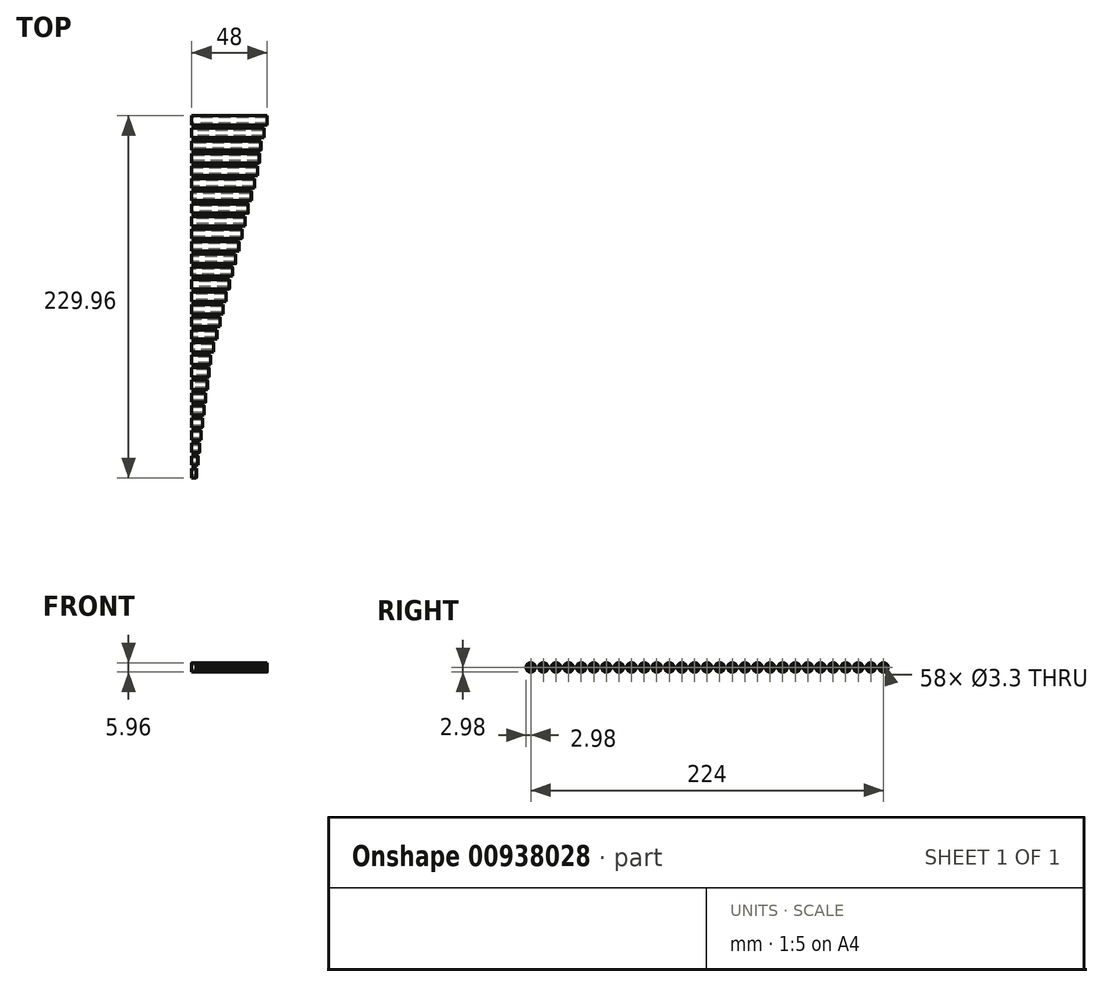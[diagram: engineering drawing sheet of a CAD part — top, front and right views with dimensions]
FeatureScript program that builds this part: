
annotation { "Feature Type Name" : "Feature", "Feature Type Description" : "" }
export const myFeature = defineFeature(function(context is Context, id is Id, definition is map)
    precondition{}
    {
        {
            var Q0;
            Q0=qCreatedBy(makeId("Right.planeOp"),FACE);
            var sketch = newSketch(context, id + "F0", { "sketchPlane" : qUnion([Q0]) });
            skCircle(sketch, "E0", {"center": v(0, 0) * mm, "radius": 1.65 * mm});
            skCircle(sketch, "E1", {"center": v(0, 0) * mm, "radius": 2.98 * mm});
            skSolve(sketch);
        }
        {
            var Q0;
            Q0=qSketchRegion(id+"F0",true);
            extrude(context, id + "F1", {"entities" : qUnion([Q0]), "depth" : 3 * mm, "offsetDistance" : 25 * mm});
        }
        {
            var Q0;
            Q0=qSketchRegion(id+"F0",true);
            extrude(context, id + "F2", {"entities" : qUnion([Q0]), "depth" : 4 * mm, "offsetDistance" : 25 * mm});
        }
        {
            var Q0;
            Q0=qSketchRegion(id+"F0",true);
            extrude(context, id + "F3", {"entities" : qUnion([Q0]), "depth" : 5 * mm, "offsetDistance" : 25 * mm});
        }
        {
            var Q0;
            Q0=qSketchRegion(id+"F0",true);
            extrude(context, id + "F4", {"entities" : qUnion([Q0]), "depth" : 6 * mm, "offsetDistance" : 25 * mm});
        }
        {
            var Q0;
            Q0=qSketchRegion(id+"F0",true);
            extrude(context, id + "F5", {"entities" : qUnion([Q0]), "depth" : 7 * mm, "offsetDistance" : 25 * mm});
        }
        {
            var Q0;
            Q0=qSketchRegion(id+"F0",true);
            extrude(context, id + "F6", {"entities" : qUnion([Q0]), "depth" : 8 * mm, "offsetDistance" : 25 * mm});
        }
        {
            var Q0;
            Q0=qSketchRegion(id+"F0",true);
            extrude(context, id + "F7", {"entities" : qUnion([Q0]), "depth" : 9 * mm, "offsetDistance" : 25 * mm});
        }
        {
            var Q0;
            Q0=qSketchRegion(id+"F0",true);
            extrude(context, id + "F8", {"entities" : qUnion([Q0]), "depth" : 10 * mm, "offsetDistance" : 25 * mm});
        }
        {
            var Q0;
            Q0=qSketchRegion(id+"F0",true);
            extrude(context, id + "F9", {"entities" : qUnion([Q0]), "depth" : 11 * mm, "offsetDistance" : 25 * mm});
        }
        {
            var Q0;
            Q0=qSketchRegion(id+"F0",true);
            extrude(context, id + "F10", {"entities" : qUnion([Q0]), "depth" : 12 * mm, "offsetDistance" : 25 * mm});
        }
        {
            var Q0;
            Q0=qSketchRegion(id+"F0",true);
            extrude(context, id + "F11", {"entities" : qUnion([Q0]), "depth" : 14 * mm, "offsetDistance" : 25 * mm});
        }
        {
            var Q0;
            Q0=qSketchRegion(id+"F0",true);
            extrude(context, id + "F12", {"entities" : qUnion([Q0]), "depth" : 16 * mm, "offsetDistance" : 25 * mm});
        }
        {
            var Q0;
            Q0=qSketchRegion(id+"F0",true);
            extrude(context, id + "F13", {"entities" : qUnion([Q0]), "depth" : 18 * mm, "offsetDistance" : 25 * mm});
        }
        {
            var Q0;
            Q0=qSketchRegion(id+"F0",true);
            extrude(context, id + "F14", {"entities" : qUnion([Q0]), "depth" : 20 * mm, "offsetDistance" : 25 * mm});
        }
        {
            var Q0;
            Q0=qSketchRegion(id+"F0",true);
            extrude(context, id + "F15", {"entities" : qUnion([Q0]), "depth" : 22 * mm, "offsetDistance" : 25 * mm});
        }
        {
            var Q0;
            Q0=qSketchRegion(id+"F0",true);
            extrude(context, id + "F16", {"entities" : qUnion([Q0]), "depth" : 24 * mm, "offsetDistance" : 25 * mm});
        }
        {
            var Q0;
            Q0=qSketchRegion(id+"F0",true);
            extrude(context, id + "F17", {"entities" : qUnion([Q0]), "depth" : 26 * mm, "offsetDistance" : 25 * mm});
        }
        {
            var Q0;
            Q0=qSketchRegion(id+"F0",true);
            extrude(context, id + "F18", {"entities" : qUnion([Q0]), "depth" : 28 * mm, "offsetDistance" : 25 * mm});
        }
        {
            var Q0;
            Q0=qSketchRegion(id+"F0",true);
            extrude(context, id + "F19", {"entities" : qUnion([Q0]), "depth" : 30 * mm, "offsetDistance" : 25 * mm});
        }
        {
            var Q0;
            Q0=qSketchRegion(id+"F0",true);
            extrude(context, id + "F20", {"entities" : qUnion([Q0]), "depth" : 32 * mm, "offsetDistance" : 25 * mm});
        }
        {
            var Q0;
            Q0=qSketchRegion(id+"F0",true);
            extrude(context, id + "F21", {"entities" : qUnion([Q0]), "depth" : 34 * mm, "offsetDistance" : 25 * mm});
        }
        {
            var Q0;
            Q0=qSketchRegion(id+"F0",true);
            extrude(context, id + "F22", {"entities" : qUnion([Q0]), "depth" : 36 * mm, "offsetDistance" : 25 * mm});
        }
        {
            var Q0;
            Q0=qSketchRegion(id+"F0",true);
            extrude(context, id + "F23", {"entities" : qUnion([Q0]), "depth" : 38 * mm, "offsetDistance" : 25 * mm});
        }
        {
            var Q0;
            Q0=qSketchRegion(id+"F0",true);
            extrude(context, id + "F24", {"entities" : qUnion([Q0]), "depth" : 40 * mm, "offsetDistance" : 25 * mm});
        }
        {
            var Q0;
            Q0=qSketchRegion(id+"F0",true);
            extrude(context, id + "F25", {"entities" : qUnion([Q0]), "depth" : 42 * mm, "offsetDistance" : 25 * mm});
        }
        {
            var Q0;
            Q0=qSketchRegion(id+"F0",true);
            extrude(context, id + "F26", {"entities" : qUnion([Q0]), "depth" : 43 * mm, "offsetDistance" : 25 * mm});
        }
        {
            var Q0;
            Q0=qSketchRegion(id+"F0",true);
            extrude(context, id + "F27", {"entities" : qUnion([Q0]), "depth" : 44 * mm, "offsetDistance" : 25 * mm});
        }
        {
            var Q0;
            Q0=qSketchRegion(id+"F0",true);
            extrude(context, id + "F28", {"entities" : qUnion([Q0]), "depth" : 46 * mm, "offsetDistance" : 25 * mm});
        }
        {
            var Q0;
            Q0=qSketchRegion(id+"F0",true);
            extrude(context, id + "F29", {"entities" : qUnion([Q0]), "depth" : 48 * mm, "offsetDistance" : 25 * mm});
        }
        {
            var Q0;
            Q0=makeQuery(id+"F1.opExtrude","CAP_EDGE",EDGE,{"disambiguationData":[OSD([sQuery(id+"F0.wireOp",EDGE,"E0")])],"isStart":false});
            var Q1;
            Q1=makeQuery(id+"F2.opExtrude","SWEPT_FACE",FACE,{"disambiguationData":[OSD([sQuery(id+"F0.wireOp",EDGE,"E0")])]});
            var Q2;
            Q2=makeQuery(id+"F3.opExtrude","CAP_EDGE",EDGE,{"disambiguationData":[OSD([sQuery(id+"F0.wireOp",EDGE,"E0")])],"isStart":false});
            var Q3;
            Q3=makeQuery(id+"F1.opExtrude","CAP_EDGE",EDGE,{"disambiguationData":[OSD([sQuery(id+"F0.wireOp",EDGE,"E0")])],"isStart":true});
            var Q4;
            Q4=makeQuery(id+"F3.opExtrude","CAP_EDGE",EDGE,{"disambiguationData":[OSD([sQuery(id+"F0.wireOp",EDGE,"E0")])],"isStart":true});
            var Q5;
            Q5=makeQuery(id+"F4.opExtrude","CAP_EDGE",EDGE,{"disambiguationData":[OSD([sQuery(id+"F0.wireOp",EDGE,"E0")])],"isStart":true});
            var Q6;
            Q6=makeQuery(id+"F4.opExtrude","CAP_EDGE",EDGE,{"disambiguationData":[OSD([sQuery(id+"F0.wireOp",EDGE,"E0")])],"isStart":false});
            var Q7;
            Q7=makeQuery(id+"F5.opExtrude","CAP_EDGE",EDGE,{"disambiguationData":[OSD([sQuery(id+"F0.wireOp",EDGE,"E0")])],"isStart":false});
            var Q8;
            Q8=makeQuery(id+"F5.opExtrude","CAP_EDGE",EDGE,{"disambiguationData":[OSD([sQuery(id+"F0.wireOp",EDGE,"E0")])],"isStart":true});
            var Q9;
            Q9=makeQuery(id+"F6.opExtrude","CAP_EDGE",EDGE,{"disambiguationData":[OSD([sQuery(id+"F0.wireOp",EDGE,"E0")])],"isStart":true});
            var Q10;
            Q10=makeQuery(id+"F6.opExtrude","CAP_EDGE",EDGE,{"disambiguationData":[OSD([sQuery(id+"F0.wireOp",EDGE,"E0")])],"isStart":false});
            var Q11;
            Q11=makeQuery(id+"F7.opExtrude","CAP_EDGE",EDGE,{"disambiguationData":[OSD([sQuery(id+"F0.wireOp",EDGE,"E0")])],"isStart":false});
            var Q12;
            Q12=makeQuery(id+"F7.opExtrude","CAP_EDGE",EDGE,{"disambiguationData":[OSD([sQuery(id+"F0.wireOp",EDGE,"E0")])],"isStart":true});
            var Q13;
            Q13=makeQuery(id+"F8.opExtrude","CAP_EDGE",EDGE,{"disambiguationData":[OSD([sQuery(id+"F0.wireOp",EDGE,"E0")])],"isStart":true});
            var Q14;
            Q14=makeQuery(id+"F8.opExtrude","CAP_EDGE",EDGE,{"disambiguationData":[OSD([sQuery(id+"F0.wireOp",EDGE,"E0")])],"isStart":false});
            var Q15;
            Q15=makeQuery(id+"F9.opExtrude","CAP_EDGE",EDGE,{"disambiguationData":[OSD([sQuery(id+"F0.wireOp",EDGE,"E0")])],"isStart":false});
            var Q16;
            Q16=makeQuery(id+"F9.opExtrude","CAP_EDGE",EDGE,{"disambiguationData":[OSD([sQuery(id+"F0.wireOp",EDGE,"E0")])],"isStart":true});
            var Q17;
            Q17=makeQuery(id+"F10.opExtrude","CAP_EDGE",EDGE,{"disambiguationData":[OSD([sQuery(id+"F0.wireOp",EDGE,"E0")])],"isStart":true});
            var Q18;
            Q18=makeQuery(id+"F10.opExtrude","CAP_EDGE",EDGE,{"disambiguationData":[OSD([sQuery(id+"F0.wireOp",EDGE,"E0")])],"isStart":false});
            var Q19;
            Q19=makeQuery(id+"F11.opExtrude","CAP_EDGE",EDGE,{"disambiguationData":[OSD([sQuery(id+"F0.wireOp",EDGE,"E0")])],"isStart":false});
            var Q20;
            Q20=makeQuery(id+"F11.opExtrude","CAP_EDGE",EDGE,{"disambiguationData":[OSD([sQuery(id+"F0.wireOp",EDGE,"E0")])],"isStart":true});
            var Q21;
            Q21=makeQuery(id+"F12.opExtrude","CAP_EDGE",EDGE,{"disambiguationData":[OSD([sQuery(id+"F0.wireOp",EDGE,"E0")])],"isStart":true});
            var Q22;
            Q22=makeQuery(id+"F12.opExtrude","CAP_EDGE",EDGE,{"disambiguationData":[OSD([sQuery(id+"F0.wireOp",EDGE,"E0")])],"isStart":false});
            var Q23;
            Q23=makeQuery(id+"F13.opExtrude","CAP_EDGE",EDGE,{"disambiguationData":[OSD([sQuery(id+"F0.wireOp",EDGE,"E0")])],"isStart":false});
            var Q24;
            Q24=makeQuery(id+"F13.opExtrude","CAP_EDGE",EDGE,{"disambiguationData":[OSD([sQuery(id+"F0.wireOp",EDGE,"E0")])],"isStart":true});
            var Q25;
            Q25=makeQuery(id+"F14.opExtrude","CAP_EDGE",EDGE,{"disambiguationData":[OSD([sQuery(id+"F0.wireOp",EDGE,"E0")])],"isStart":true});
            var Q26;
            Q26=makeQuery(id+"F14.opExtrude","CAP_EDGE",EDGE,{"disambiguationData":[OSD([sQuery(id+"F0.wireOp",EDGE,"E0")])],"isStart":false});
            var Q27;
            Q27=makeQuery(id+"F15.opExtrude","CAP_EDGE",EDGE,{"disambiguationData":[OSD([sQuery(id+"F0.wireOp",EDGE,"E0")])],"isStart":false});
            var Q28;
            Q28=makeQuery(id+"F15.opExtrude","CAP_EDGE",EDGE,{"disambiguationData":[OSD([sQuery(id+"F0.wireOp",EDGE,"E0")])],"isStart":true});
            var Q29;
            Q29=makeQuery(id+"F16.opExtrude","CAP_EDGE",EDGE,{"disambiguationData":[OSD([sQuery(id+"F0.wireOp",EDGE,"E0")])],"isStart":true});
            var Q30;
            Q30=makeQuery(id+"F16.opExtrude","CAP_EDGE",EDGE,{"disambiguationData":[OSD([sQuery(id+"F0.wireOp",EDGE,"E0")])],"isStart":false});
            var Q31;
            Q31=makeQuery(id+"F17.opExtrude","CAP_EDGE",EDGE,{"disambiguationData":[OSD([sQuery(id+"F0.wireOp",EDGE,"E0")])],"isStart":false});
            var Q32;
            Q32=makeQuery(id+"F17.opExtrude","CAP_EDGE",EDGE,{"disambiguationData":[OSD([sQuery(id+"F0.wireOp",EDGE,"E0")])],"isStart":true});
            var Q33;
            Q33=makeQuery(id+"F18.opExtrude","CAP_EDGE",EDGE,{"disambiguationData":[OSD([sQuery(id+"F0.wireOp",EDGE,"E0")])],"isStart":true});
            var Q34;
            Q34=makeQuery(id+"F18.opExtrude","CAP_EDGE",EDGE,{"disambiguationData":[OSD([sQuery(id+"F0.wireOp",EDGE,"E0")])],"isStart":false});
            var Q35;
            Q35=makeQuery(id+"F19.opExtrude","CAP_EDGE",EDGE,{"disambiguationData":[OSD([sQuery(id+"F0.wireOp",EDGE,"E0")])],"isStart":false});
            var Q36;
            Q36=makeQuery(id+"F19.opExtrude","CAP_EDGE",EDGE,{"disambiguationData":[OSD([sQuery(id+"F0.wireOp",EDGE,"E0")])],"isStart":true});
            var Q37;
            Q37=makeQuery(id+"F20.opExtrude","CAP_EDGE",EDGE,{"disambiguationData":[OSD([sQuery(id+"F0.wireOp",EDGE,"E0")])],"isStart":true});
            var Q38;
            Q38=makeQuery(id+"F20.opExtrude","CAP_EDGE",EDGE,{"disambiguationData":[OSD([sQuery(id+"F0.wireOp",EDGE,"E0")])],"isStart":false});
            var Q39;
            Q39=makeQuery(id+"F21.opExtrude","CAP_EDGE",EDGE,{"disambiguationData":[OSD([sQuery(id+"F0.wireOp",EDGE,"E0")])],"isStart":false});
            var Q40;
            Q40=makeQuery(id+"F21.opExtrude","CAP_EDGE",EDGE,{"disambiguationData":[OSD([sQuery(id+"F0.wireOp",EDGE,"E0")])],"isStart":true});
            var Q41;
            Q41=makeQuery(id+"F22.opExtrude","CAP_EDGE",EDGE,{"disambiguationData":[OSD([sQuery(id+"F0.wireOp",EDGE,"E0")])],"isStart":true});
            var Q42;
            Q42=makeQuery(id+"F22.opExtrude","CAP_EDGE",EDGE,{"disambiguationData":[OSD([sQuery(id+"F0.wireOp",EDGE,"E0")])],"isStart":false});
            var Q43;
            Q43=makeQuery(id+"F23.opExtrude","CAP_EDGE",EDGE,{"disambiguationData":[OSD([sQuery(id+"F0.wireOp",EDGE,"E0")])],"isStart":false});
            var Q44;
            Q44=makeQuery(id+"F23.opExtrude","CAP_EDGE",EDGE,{"disambiguationData":[OSD([sQuery(id+"F0.wireOp",EDGE,"E0")])],"isStart":true});
            var Q45;
            Q45=makeQuery(id+"F24.opExtrude","CAP_EDGE",EDGE,{"disambiguationData":[OSD([sQuery(id+"F0.wireOp",EDGE,"E0")])],"isStart":true});
            var Q46;
            Q46=makeQuery(id+"F24.opExtrude","SWEPT_FACE",FACE,{"disambiguationData":[OSD([sQuery(id+"F0.wireOp",EDGE,"E0")])]});
            var Q47;
            Q47=makeQuery(id+"F25.opExtrude","CAP_EDGE",EDGE,{"disambiguationData":[OSD([sQuery(id+"F0.wireOp",EDGE,"E0")])],"isStart":false});
            var Q48;
            Q48=makeQuery(id+"F25.opExtrude","CAP_EDGE",EDGE,{"disambiguationData":[OSD([sQuery(id+"F0.wireOp",EDGE,"E0")])],"isStart":true});
            var Q49;
            Q49=makeQuery(id+"F26.opExtrude","CAP_EDGE",EDGE,{"disambiguationData":[OSD([sQuery(id+"F0.wireOp",EDGE,"E0")])],"isStart":true});
            var Q50;
            Q50=makeQuery(id+"F26.opExtrude","CAP_EDGE",EDGE,{"disambiguationData":[OSD([sQuery(id+"F0.wireOp",EDGE,"E0")])],"isStart":false});
            var Q51;
            Q51=makeQuery(id+"F27.opExtrude","CAP_EDGE",EDGE,{"disambiguationData":[OSD([sQuery(id+"F0.wireOp",EDGE,"E0")])],"isStart":false});
            var Q52;
            Q52=makeQuery(id+"F27.opExtrude","CAP_EDGE",EDGE,{"disambiguationData":[OSD([sQuery(id+"F0.wireOp",EDGE,"E0")])],"isStart":true});
            var Q53;
            Q53=makeQuery(id+"F28.opExtrude","CAP_EDGE",EDGE,{"disambiguationData":[OSD([sQuery(id+"F0.wireOp",EDGE,"E0")])],"isStart":true});
            var Q54;
            Q54=makeQuery(id+"F28.opExtrude","CAP_EDGE",EDGE,{"disambiguationData":[OSD([sQuery(id+"F0.wireOp",EDGE,"E0")])],"isStart":false});
            var Q55;
            Q55=makeQuery(id+"F29.opExtrude","CAP_EDGE",EDGE,{"disambiguationData":[OSD([sQuery(id+"F0.wireOp",EDGE,"E0")])],"isStart":false});
            var Q56;
            Q56=makeQuery(id+"F29.opExtrude","CAP_EDGE",EDGE,{"disambiguationData":[OSD([sQuery(id+"F0.wireOp",EDGE,"E0")])],"isStart":true});
            chamfer(context, id + "F30", {"entities" : qUnion([Q0, Q1, Q2, Q3, Q4, Q5, Q6, Q7, Q8, Q9, Q10, Q11, Q12, Q13, Q14, Q15, Q16, Q17, Q18, Q19, Q20, Q21, Q22, Q23, Q24, Q25, Q26, Q27, Q28, Q29, Q30, Q31, Q32, Q33, Q34, Q35, Q36, Q37, Q38, Q39, Q40, Q41, Q42, Q43, Q44, Q45, Q46, Q47, Q48, Q49, Q50, Q51, Q52, Q53, Q54, Q55, Q56]), "width" : 0.35 * mm, "tangentPropagation" : true});
        }
        {
            var Q0;
            Q0=makeQuery(id+"F29.opExtrude","CAP_EDGE",EDGE,{"disambiguationData":[OSD([sQuery(id+"F0.wireOp",EDGE,"E1")])],"isStart":false});
            var Q1;
            Q1=makeQuery(id+"F28.opExtrude","CAP_EDGE",EDGE,{"disambiguationData":[OSD([sQuery(id+"F0.wireOp",EDGE,"E1")])],"isStart":false});
            var Q2;
            Q2=makeQuery(id+"F27.opExtrude","CAP_EDGE",EDGE,{"disambiguationData":[OSD([sQuery(id+"F0.wireOp",EDGE,"E1")])],"isStart":false});
            var Q3;
            Q3=makeQuery(id+"F26.opExtrude","CAP_EDGE",EDGE,{"disambiguationData":[OSD([sQuery(id+"F0.wireOp",EDGE,"E1")])],"isStart":false});
            var Q4;
            Q4=makeQuery(id+"F25.opExtrude","CAP_EDGE",EDGE,{"disambiguationData":[OSD([sQuery(id+"F0.wireOp",EDGE,"E1")])],"isStart":false});
            var Q5;
            Q5=makeQuery(id+"F24.opExtrude","CAP_EDGE",EDGE,{"disambiguationData":[OSD([sQuery(id+"F0.wireOp",EDGE,"E1")])],"isStart":false});
            var Q6;
            Q6=makeQuery(id+"F23.opExtrude","CAP_EDGE",EDGE,{"disambiguationData":[OSD([sQuery(id+"F0.wireOp",EDGE,"E1")])],"isStart":false});
            var Q7;
            Q7=makeQuery(id+"F22.opExtrude","CAP_EDGE",EDGE,{"disambiguationData":[OSD([sQuery(id+"F0.wireOp",EDGE,"E1")])],"isStart":false});
            var Q8;
            Q8=makeQuery(id+"F21.opExtrude","CAP_EDGE",EDGE,{"disambiguationData":[OSD([sQuery(id+"F0.wireOp",EDGE,"E1")])],"isStart":false});
            var Q9;
            Q9=makeQuery(id+"F20.opExtrude","CAP_EDGE",EDGE,{"disambiguationData":[OSD([sQuery(id+"F0.wireOp",EDGE,"E1")])],"isStart":false});
            var Q10;
            Q10=makeQuery(id+"F19.opExtrude","CAP_EDGE",EDGE,{"disambiguationData":[OSD([sQuery(id+"F0.wireOp",EDGE,"E1")])],"isStart":false});
            var Q11;
            Q11=makeQuery(id+"F18.opExtrude","CAP_EDGE",EDGE,{"disambiguationData":[OSD([sQuery(id+"F0.wireOp",EDGE,"E1")])],"isStart":false});
            var Q12;
            Q12=makeQuery(id+"F17.opExtrude","CAP_EDGE",EDGE,{"disambiguationData":[OSD([sQuery(id+"F0.wireOp",EDGE,"E1")])],"isStart":false});
            var Q13;
            Q13=makeQuery(id+"F16.opExtrude","CAP_EDGE",EDGE,{"disambiguationData":[OSD([sQuery(id+"F0.wireOp",EDGE,"E1")])],"isStart":false});
            var Q14;
            Q14=makeQuery(id+"F15.opExtrude","CAP_EDGE",EDGE,{"disambiguationData":[OSD([sQuery(id+"F0.wireOp",EDGE,"E1")])],"isStart":false});
            var Q15;
            Q15=makeQuery(id+"F14.opExtrude","CAP_EDGE",EDGE,{"disambiguationData":[OSD([sQuery(id+"F0.wireOp",EDGE,"E1")])],"isStart":false});
            var Q16;
            Q16=makeQuery(id+"F24.opExtrude","SWEPT_FACE",FACE,{"disambiguationData":[OSD([sQuery(id+"F0.wireOp",EDGE,"E1")])]});
            var Q17;
            Q17=makeQuery(id+"F12.opExtrude","CAP_EDGE",EDGE,{"disambiguationData":[OSD([sQuery(id+"F0.wireOp",EDGE,"E1")])],"isStart":false});
            var Q18;
            Q18=makeQuery(id+"F13.opExtrude","CAP_EDGE",EDGE,{"disambiguationData":[OSD([sQuery(id+"F0.wireOp",EDGE,"E1")])],"isStart":false});
            var Q19;
            Q19=makeQuery(id+"F11.opExtrude","CAP_EDGE",EDGE,{"disambiguationData":[OSD([sQuery(id+"F0.wireOp",EDGE,"E1")])],"isStart":false});
            var Q20;
            Q20=makeQuery(id+"F10.opExtrude","CAP_EDGE",EDGE,{"disambiguationData":[OSD([sQuery(id+"F0.wireOp",EDGE,"E1")])],"isStart":false});
            var Q21;
            Q21=makeQuery(id+"F9.opExtrude","CAP_EDGE",EDGE,{"disambiguationData":[OSD([sQuery(id+"F0.wireOp",EDGE,"E1")])],"isStart":false});
            var Q22;
            Q22=makeQuery(id+"F8.opExtrude","CAP_EDGE",EDGE,{"disambiguationData":[OSD([sQuery(id+"F0.wireOp",EDGE,"E1")])],"isStart":false});
            var Q23;
            Q23=makeQuery(id+"F7.opExtrude","CAP_EDGE",EDGE,{"disambiguationData":[OSD([sQuery(id+"F0.wireOp",EDGE,"E1")])],"isStart":false});
            var Q24;
            Q24=makeQuery(id+"F6.opExtrude","CAP_EDGE",EDGE,{"disambiguationData":[OSD([sQuery(id+"F0.wireOp",EDGE,"E1")])],"isStart":false});
            var Q25;
            Q25=makeQuery(id+"F5.opExtrude","CAP_EDGE",EDGE,{"disambiguationData":[OSD([sQuery(id+"F0.wireOp",EDGE,"E1")])],"isStart":false});
            var Q26;
            Q26=makeQuery(id+"F4.opExtrude","CAP_EDGE",EDGE,{"disambiguationData":[OSD([sQuery(id+"F0.wireOp",EDGE,"E1")])],"isStart":false});
            var Q27;
            Q27=makeQuery(id+"F3.opExtrude","CAP_EDGE",EDGE,{"disambiguationData":[OSD([sQuery(id+"F0.wireOp",EDGE,"E1")])],"isStart":false});
            var Q28;
            Q28=makeQuery(id+"F2.opExtrude","CAP_EDGE",EDGE,{"disambiguationData":[OSD([sQuery(id+"F0.wireOp",EDGE,"E1")])],"isStart":false});
            var Q29;
            Q29=makeQuery(id+"F1.opExtrude","CAP_EDGE",EDGE,{"disambiguationData":[OSD([sQuery(id+"F0.wireOp",EDGE,"E1")])],"isStart":false});
            chamfer(context, id + "F31", {"entities" : qUnion([Q0, Q1, Q2, Q3, Q4, Q5, Q6, Q7, Q8, Q9, Q10, Q11, Q12, Q13, Q14, Q15, Q16, Q17, Q18, Q19, Q20, Q21, Q22, Q23, Q24, Q25, Q26, Q27, Q28, Q29]), "width" : 0.1 * mm, "tangentPropagation" : true});
        }
        {
            var Q0;
            Q0=qCreatedBy(makeId("Front.planeOp"),FACE);
            var sketch = newSketch(context, id + "F32", { "sketchPlane" : qUnion([Q0]) });
            skLineSegment(sketch, "E2", {"start": v(2.9, -2.98) * mm, "end": v(0, -2.98) * mm, "construction": true});
            skLineSegment(sketch, "E3", {"start": v(0, 2.98) * mm, "end": v(2.9, 2.98) * mm, "construction": true});
            skLineSegment(sketch, "E4", {"start": v(0, 2.88) * mm, "end": v(0.1, 2.98) * mm});
            skLineSegment(sketch, "E5", {"start": v(0.1, 2.98) * mm, "end": v(0, 2.98) * mm});
            skLineSegment(sketch, "E6", {"start": v(0, 2.98) * mm, "end": v(0, 2.88) * mm});
            skLineSegment(sketch, "E7", {"start": v(0, 2.98) * mm, "end": v(0.1, 2.98) * mm});
            skLineSegment(sketch, "E8", {"start": v(0, 0) * mm, "end": v(-2.68, 0) * mm, "construction": true});
            skSolve(sketch);
        }
        {
            var Q0;
            Q0=qSketchRegion(id+"F32",true);
            var Q1;
            Q1=sQuery(id+"F32.wireOp",EDGE,"E8");
            revolve(context, id + "F33", {"operationType" : NewBodyOperationType.REMOVE, "surfaceOperationType" : NewSurfaceOperationType.NEW, "entities" : qUnion([Q0]), "axis" : qUnion([Q1]), "revolveType" : RevolveType.FULL, "oppositeDirection" : true});
        }
        {
            var Q0;
            Q0=makeQuery(id+"F2.opExtrude","SWEPT_BODY",BODY,{"disambiguationData":[OSD([sQuery(id+"F0.wireOp",EDGE,"E0"),sQuery(id+"F0.wireOp",EDGE,"E1")])]});
            transform(context, id + "F34", {"entities" : qUnion([Q0]), "transformType" : TransformType.TRANSLATION_3D, "dx" : 0 * mm, "dy" : 8 * mm, "dz" : 0 * mm, "makeCopy" : false});
        }
        {
            var Q0;
            Q0=makeQuery(id+"F3.opExtrude","SWEPT_BODY",BODY,{"disambiguationData":[OSD([sQuery(id+"F0.wireOp",EDGE,"E0"),sQuery(id+"F0.wireOp",EDGE,"E1")])]});
            transform(context, id + "F35", {"entities" : qUnion([Q0]), "transformType" : TransformType.TRANSLATION_3D, "dx" : 0 * mm, "dy" : 16 * mm, "dz" : 0 * mm, "makeCopy" : false});
        }
        {
            var Q0;
            Q0=makeQuery(id+"F4.opExtrude","SWEPT_BODY",BODY,{"disambiguationData":[OSD([sQuery(id+"F0.wireOp",EDGE,"E0"),sQuery(id+"F0.wireOp",EDGE,"E1")])]});
            transform(context, id + "F36", {"entities" : qUnion([Q0]), "transformType" : TransformType.TRANSLATION_3D, "dx" : 0 * mm, "dy" : 24 * mm, "dz" : 0 * mm, "makeCopy" : false});
        }
        {
            var Q0;
            Q0=makeQuery(id+"F5.opExtrude","SWEPT_BODY",BODY,{"disambiguationData":[OSD([sQuery(id+"F0.wireOp",EDGE,"E0"),sQuery(id+"F0.wireOp",EDGE,"E1")])]});
            transform(context, id + "F37", {"entities" : qUnion([Q0]), "transformType" : TransformType.TRANSLATION_3D, "dx" : 0 * mm, "dy" : 32 * mm, "dz" : 0 * mm, "makeCopy" : false});
        }
        {
            var Q0;
            Q0=makeQuery(id+"F6.opExtrude","SWEPT_BODY",BODY,{"disambiguationData":[OSD([sQuery(id+"F0.wireOp",EDGE,"E0"),sQuery(id+"F0.wireOp",EDGE,"E1")])]});
            transform(context, id + "F38", {"entities" : qUnion([Q0]), "transformType" : TransformType.TRANSLATION_3D, "dx" : 0 * mm, "dy" : 40 * mm, "dz" : 0 * mm, "makeCopy" : false});
        }
        {
            var Q0;
            Q0=makeQuery(id+"F7.opExtrude","SWEPT_BODY",BODY,{"disambiguationData":[OSD([sQuery(id+"F0.wireOp",EDGE,"E0"),sQuery(id+"F0.wireOp",EDGE,"E1")])]});
            transform(context, id + "F39", {"entities" : qUnion([Q0]), "transformType" : TransformType.TRANSLATION_3D, "dx" : 0 * mm, "dy" : 48 * mm, "dz" : 0 * mm, "makeCopy" : false});
        }
        {
            var Q0;
            Q0=makeQuery(id+"F8.opExtrude","SWEPT_BODY",BODY,{"disambiguationData":[OSD([sQuery(id+"F0.wireOp",EDGE,"E0"),sQuery(id+"F0.wireOp",EDGE,"E1")])]});
            transform(context, id + "F40", {"entities" : qUnion([Q0]), "transformType" : TransformType.TRANSLATION_3D, "dx" : 0 * mm, "dy" : 56 * mm, "dz" : 0 * mm, "makeCopy" : false});
        }
        {
            var Q0;
            Q0=makeQuery(id+"F9.opExtrude","SWEPT_BODY",BODY,{"disambiguationData":[OSD([sQuery(id+"F0.wireOp",EDGE,"E0"),sQuery(id+"F0.wireOp",EDGE,"E1")])]});
            transform(context, id + "F41", {"entities" : qUnion([Q0]), "transformType" : TransformType.TRANSLATION_3D, "dx" : 0 * mm, "dy" : 64 * mm, "dz" : 0 * mm, "makeCopy" : false});
        }
        {
            var Q0;
            Q0=makeQuery(id+"F10.opExtrude","SWEPT_BODY",BODY,{"disambiguationData":[OSD([sQuery(id+"F0.wireOp",EDGE,"E0"),sQuery(id+"F0.wireOp",EDGE,"E1")])]});
            transform(context, id + "F42", {"entities" : qUnion([Q0]), "transformType" : TransformType.TRANSLATION_3D, "dx" : 0 * mm, "dy" : 72 * mm, "dz" : 0 * mm, "makeCopy" : false});
        }
        {
            var Q0;
            Q0=makeQuery(id+"F11.opExtrude","SWEPT_BODY",BODY,{"disambiguationData":[OSD([sQuery(id+"F0.wireOp",EDGE,"E0"),sQuery(id+"F0.wireOp",EDGE,"E1")])]});
            transform(context, id + "F43", {"entities" : qUnion([Q0]), "transformType" : TransformType.TRANSLATION_3D, "dx" : 0 * mm, "dy" : 80 * mm, "dz" : 0 * mm, "makeCopy" : false});
        }
        {
            var Q0;
            Q0=makeQuery(id+"F12.opExtrude","SWEPT_BODY",BODY,{"disambiguationData":[OSD([sQuery(id+"F0.wireOp",EDGE,"E0"),sQuery(id+"F0.wireOp",EDGE,"E1")])]});
            transform(context, id + "F44", {"entities" : qUnion([Q0]), "transformType" : TransformType.TRANSLATION_3D, "dx" : 0 * mm, "dy" : 88 * mm, "dz" : 0 * mm, "makeCopy" : false});
        }
        {
            var Q0;
            Q0=makeQuery(id+"F13.opExtrude","SWEPT_BODY",BODY,{"disambiguationData":[OSD([sQuery(id+"F0.wireOp",EDGE,"E0"),sQuery(id+"F0.wireOp",EDGE,"E1")])]});
            transform(context, id + "F45", {"entities" : qUnion([Q0]), "transformType" : TransformType.TRANSLATION_3D, "dx" : 0 * mm, "dy" : 96 * mm, "dz" : 0 * mm, "makeCopy" : false});
        }
        {
            var Q0;
            Q0=makeQuery(id+"F14.opExtrude","SWEPT_BODY",BODY,{"disambiguationData":[OSD([sQuery(id+"F0.wireOp",EDGE,"E0"),sQuery(id+"F0.wireOp",EDGE,"E1")])]});
            transform(context, id + "F46", {"entities" : qUnion([Q0]), "transformType" : TransformType.TRANSLATION_3D, "dx" : 0 * mm, "dy" : 104 * mm, "dz" : 0 * mm, "makeCopy" : false});
        }
        {
            var Q0;
            Q0=makeQuery(id+"F15.opExtrude","SWEPT_BODY",BODY,{"disambiguationData":[OSD([sQuery(id+"F0.wireOp",EDGE,"E0"),sQuery(id+"F0.wireOp",EDGE,"E1")])]});
            transform(context, id + "F47", {"entities" : qUnion([Q0]), "transformType" : TransformType.TRANSLATION_3D, "dx" : 0 * mm, "dy" : 112 * mm, "dz" : 0 * mm, "makeCopy" : false});
        }
        {
            var Q0;
            Q0=makeQuery(id+"F16.opExtrude","SWEPT_BODY",BODY,{"disambiguationData":[OSD([sQuery(id+"F0.wireOp",EDGE,"E0"),sQuery(id+"F0.wireOp",EDGE,"E1")])]});
            transform(context, id + "F48", {"entities" : qUnion([Q0]), "transformType" : TransformType.TRANSLATION_3D, "dx" : 0 * mm, "dy" : 120 * mm, "dz" : 0 * mm, "makeCopy" : false});
        }
        {
            var Q0;
            Q0=makeQuery(id+"F17.opExtrude","SWEPT_BODY",BODY,{"disambiguationData":[OSD([sQuery(id+"F0.wireOp",EDGE,"E0"),sQuery(id+"F0.wireOp",EDGE,"E1")])]});
            transform(context, id + "F49", {"entities" : qUnion([Q0]), "transformType" : TransformType.TRANSLATION_3D, "dx" : 0 * mm, "dy" : 128 * mm, "dz" : 0 * mm, "makeCopy" : false});
        }
        {
            var Q0;
            Q0=makeQuery(id+"F18.opExtrude","SWEPT_BODY",BODY,{"disambiguationData":[OSD([sQuery(id+"F0.wireOp",EDGE,"E0"),sQuery(id+"F0.wireOp",EDGE,"E1")])]});
            transform(context, id + "F50", {"entities" : qUnion([Q0]), "transformType" : TransformType.TRANSLATION_3D, "dx" : 0 * mm, "dy" : 136 * mm, "dz" : 0 * mm, "makeCopy" : false});
        }
        {
            var Q0;
            Q0=makeQuery(id+"F19.opExtrude","SWEPT_BODY",BODY,{"disambiguationData":[OSD([sQuery(id+"F0.wireOp",EDGE,"E0"),sQuery(id+"F0.wireOp",EDGE,"E1")])]});
            transform(context, id + "F51", {"entities" : qUnion([Q0]), "transformType" : TransformType.TRANSLATION_3D, "dx" : 0 * mm, "dy" : 144 * mm, "dz" : 0 * mm, "makeCopy" : false});
        }
        {
            var Q0;
            Q0=makeQuery(id+"F20.opExtrude","SWEPT_BODY",BODY,{"disambiguationData":[OSD([sQuery(id+"F0.wireOp",EDGE,"E0"),sQuery(id+"F0.wireOp",EDGE,"E1")])]});
            transform(context, id + "F52", {"entities" : qUnion([Q0]), "transformType" : TransformType.TRANSLATION_3D, "dx" : 0 * mm, "dy" : 152 * mm, "dz" : 0 * mm, "makeCopy" : false});
        }
        {
            var Q0;
            Q0=makeQuery(id+"F21.opExtrude","SWEPT_BODY",BODY,{"disambiguationData":[OSD([sQuery(id+"F0.wireOp",EDGE,"E0"),sQuery(id+"F0.wireOp",EDGE,"E1")])]});
            transform(context, id + "F53", {"entities" : qUnion([Q0]), "transformType" : TransformType.TRANSLATION_3D, "dx" : 0 * mm, "dy" : 160 * mm, "dz" : 0 * mm, "makeCopy" : false});
        }
        {
            var Q0;
            Q0=makeQuery(id+"F22.opExtrude","SWEPT_BODY",BODY,{"disambiguationData":[OSD([sQuery(id+"F0.wireOp",EDGE,"E0"),sQuery(id+"F0.wireOp",EDGE,"E1")])]});
            transform(context, id + "F54", {"entities" : qUnion([Q0]), "transformType" : TransformType.TRANSLATION_3D, "dx" : 0 * mm, "dy" : 168 * mm, "dz" : 0 * mm, "makeCopy" : false});
        }
        {
            var Q0;
            Q0=makeQuery(id+"F23.opExtrude","SWEPT_BODY",BODY,{"disambiguationData":[OSD([sQuery(id+"F0.wireOp",EDGE,"E0"),sQuery(id+"F0.wireOp",EDGE,"E1")])]});
            transform(context, id + "F55", {"entities" : qUnion([Q0]), "transformType" : TransformType.TRANSLATION_3D, "dx" : 0 * mm, "dy" : 176 * mm, "dz" : 0 * mm, "makeCopy" : false});
        }
        {
            var Q0;
            Q0=makeQuery(id+"F24.opExtrude","SWEPT_BODY",BODY,{"disambiguationData":[OSD([sQuery(id+"F0.wireOp",EDGE,"E0"),sQuery(id+"F0.wireOp",EDGE,"E1")])]});
            transform(context, id + "F56", {"entities" : qUnion([Q0]), "transformType" : TransformType.TRANSLATION_3D, "dx" : 0 * mm, "dy" : 184 * mm, "dz" : 0 * mm, "makeCopy" : false});
        }
        {
            var Q0;
            Q0=makeQuery(id+"F25.opExtrude","SWEPT_BODY",BODY,{"disambiguationData":[OSD([sQuery(id+"F0.wireOp",EDGE,"E0"),sQuery(id+"F0.wireOp",EDGE,"E1")])]});
            transform(context, id + "F57", {"entities" : qUnion([Q0]), "transformType" : TransformType.TRANSLATION_3D, "dx" : 0 * mm, "dy" : 192 * mm, "dz" : 0 * mm, "makeCopy" : false});
        }
        {
            var Q0;
            Q0=makeQuery(id+"F26.opExtrude","SWEPT_BODY",BODY,{"disambiguationData":[OSD([sQuery(id+"F0.wireOp",EDGE,"E0"),sQuery(id+"F0.wireOp",EDGE,"E1")])]});
            transform(context, id + "F58", {"entities" : qUnion([Q0]), "transformType" : TransformType.TRANSLATION_3D, "dx" : 0 * mm, "dy" : 200 * mm, "dz" : 0 * mm, "makeCopy" : false});
        }
        {
            var Q0;
            Q0=makeQuery(id+"F27.opExtrude","SWEPT_BODY",BODY,{"disambiguationData":[OSD([sQuery(id+"F0.wireOp",EDGE,"E0"),sQuery(id+"F0.wireOp",EDGE,"E1")])]});
            transform(context, id + "F59", {"entities" : qUnion([Q0]), "transformType" : TransformType.TRANSLATION_3D, "dx" : 0 * mm, "dy" : 208 * mm, "dz" : 0 * mm, "makeCopy" : false});
        }
        {
            var Q0;
            Q0=makeQuery(id+"F28.opExtrude","SWEPT_BODY",BODY,{"disambiguationData":[OSD([sQuery(id+"F0.wireOp",EDGE,"E0"),sQuery(id+"F0.wireOp",EDGE,"E1")])]});
            transform(context, id + "F60", {"entities" : qUnion([Q0]), "transformType" : TransformType.TRANSLATION_3D, "dx" : 0 * mm, "dy" : 216 * mm, "dz" : 0 * mm, "makeCopy" : false});
        }
        {
            var Q0;
            Q0=makeQuery(id+"F29.opExtrude","SWEPT_BODY",BODY,{"disambiguationData":[OSD([sQuery(id+"F0.wireOp",EDGE,"E0"),sQuery(id+"F0.wireOp",EDGE,"E1")])]});
            transform(context, id + "F61", {"entities" : qUnion([Q0]), "transformType" : TransformType.TRANSLATION_3D, "dx" : 0 * mm, "dy" : 224 * mm, "dz" : 0 * mm, "makeCopy" : false});
        }
    });
